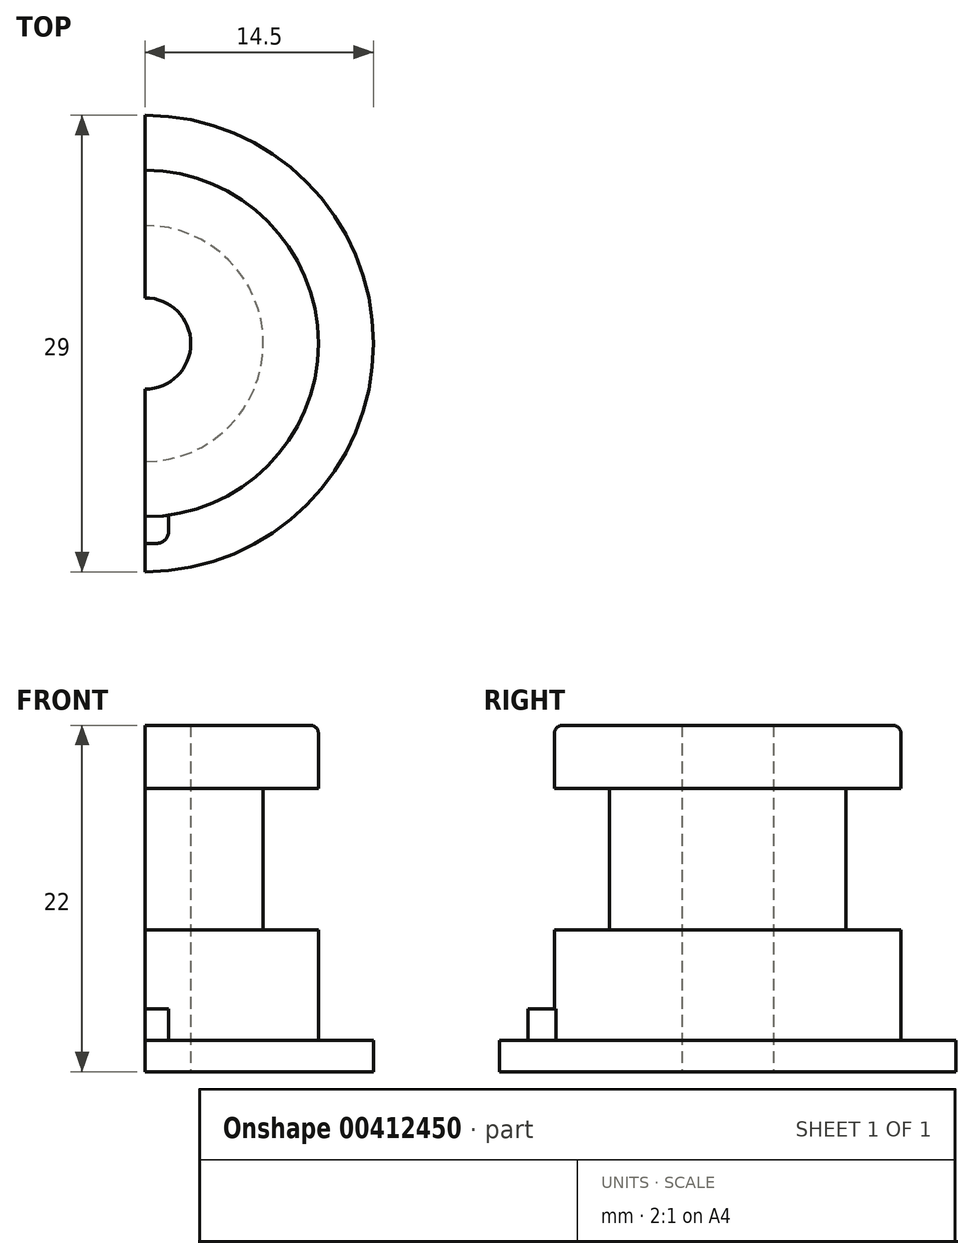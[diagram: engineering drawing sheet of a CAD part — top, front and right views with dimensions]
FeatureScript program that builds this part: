
annotation { "Feature Type Name" : "Feature", "Feature Type Description" : "" }
export const myFeature = defineFeature(function(context is Context, id is Id, definition is map)
    precondition{}
    {
        {
            var Q0;
            Q0=qCreatedBy(makeId("Top.planeOp"),FACE);
            var sketch = newSketch(context, id + "F0", { "sketchPlane" : qUnion([Q0])});
            skCircle(sketch, "E0", {"center": v(0, 0) * mm, "radius": 14.5 * mm});
            skSolve(sketch);
        }
        {
            var Q0;
            Q0=qSketchRegion(id+"F0",true);
            extrude(context, id + "F1", {"entities" : qUnion([Q0]), "depth" : 2 * mm});
        }
        {
            var Q0;
            Q0=makeQuery(id+"F1.opExtrude","CAP_FACE",FACE,{"disambiguationData":[OSD([sQuery(id+"F0.wireOp",EDGE,"E0")])],"isStart":false});
            var sketch = newSketch(context, id + "F2", { "sketchPlane" : qUnion([Q0])});
            skCircle(sketch, "E1", {"center": v(0, 0) * mm, "radius": 11 * mm});
            skSolve(sketch);
        }
        {
            var Q0;
            Q0=qSketchRegion(id+"F2",true);
            extrude(context, id + "F3", {"entities" : qUnion([Q0]), "operationType" : NewBodyOperationType.ADD, "depth" : 20 * mm});
        }
        {
            var Q0;
            Q0=makeQuery(id+"F1.opExtrude","CAP_FACE",FACE,{"disambiguationData":[OSD([sQuery(id+"F0.wireOp",EDGE,"E0")])],"isStart":true});
            var sketch = newSketch(context, id + "F4", { "sketchPlane" : qUnion([Q0])});
            skCircle(sketch, "E2", {"center": v(0, 0) * mm, "radius": 2.9 * mm});
            skSolve(sketch);
        }
        {
            var Q0;
            Q0=qSketchRegion(id+"F4",true);
            extrude(context, id + "F5", {"entities" : qUnion([Q0]), "operationType" : NewBodyOperationType.REMOVE, "endBound" : BoundingType.THROUGH_ALL, "oppositeDirection" : true, "depth" : 25 * mm});
        }
        {
            var Q0;
            Q0=makeQuery(id+"F1.opExtrude","CAP_FACE",FACE,{"disambiguationData":[OSD([sQuery(id+"F0.wireOp",EDGE,"E0")])],"isStart":false});
            var sketch = newSketch(context, id + "F6", { "sketchPlane" : qUnion([Q0])});
            skLineSegment(sketch, "E3.bottom", {"start": v(-1.5, -9.3) * mm, "end": v(1.5, -9.3) * mm});
            skLineSegment(sketch, "E3.top", {"start": v(-1.5, -12.7) * mm, "end": v(1.5, -12.7) * mm});
            skLineSegment(sketch, "E3.left", {"start": v(-1.5, -9.3) * mm, "end": v(-1.5, -12.7) * mm});
            skLineSegment(sketch, "E3.right", {"start": v(1.5, -9.3) * mm, "end": v(1.5, -12.7) * mm});
            skPoint(sketch, "E3.middle", {"position": v(0, -11) * mm});
            skSolve(sketch);
        }
        {
            var Q0;
            {var subQ0=sQuery(id+"F6.wireOp",EDGE,"E3.top");Q0=makeQuery(id+"F6.imprint","IMPRINT",FACE,{"disambiguationData":[TD([[makeQuery(id+"F6.imprint","IMPRINT",EDGE,{"derivedFrom":subQ0}),1.0]])]});}
            extrude(context, id + "F7", {"entities" : qUnion([Q0]), "operationType" : NewBodyOperationType.ADD, "depth" : 2 * mm});
        }
        {
            var Q0;
            Q0=makeQuery(id+"F7.opExtrude","SWEPT_EDGE",EDGE,{"disambiguationData":[OSD([sQuery(id+"F6.wireOp",EDGE,"E3.top"),sQuery(id+"F6.wireOp",EDGE,"E3.left")])]});
            var Q1;
            Q1=makeQuery(id+"F7.opExtrude","SWEPT_EDGE",EDGE,{"disambiguationData":[OSD([sQuery(id+"F6.wireOp",EDGE,"E3.top"),sQuery(id+"F6.wireOp",EDGE,"E3.right")])]});
            fillet(context, id + "F8", {"entities" : qUnion([Q0, Q1]), "radius" : 0.8 * mm, "tangentPropagation" : true, "allowEdgeOverflow" : false});
        }
        {
            var Q0;
            Q0=makeQuery(id+"F3.opExtrude","CAP_EDGE",EDGE,{"disambiguationData":[OSD([sQuery(id+"F2.wireOp",EDGE,"E1")])],"isStart":false});
            fillet(context, id + "F9", {"entities" : qUnion([Q0]), "radius" : 0.5 * mm, "tangentPropagation" : true, "allowEdgeOverflow" : false});
        }
        {
            var Q0;
            Q0=qCreatedBy(makeId("Front.planeOp"),FACE);
            var sketch = newSketch(context, id + "F10", { "sketchPlane" : qUnion([Q0])});
            skLineSegment(sketch, "E4", {"start": v(11, 2) * mm, "end": v(11, 4.1) * mm});
            skLineSegment(sketch, "E5", {"start": v(11, 4.1) * mm, "end": v(9.18, 3.05) * mm});
            skLineSegment(sketch, "E6", {"start": v(9.18, 3.05) * mm, "end": v(11, 2) * mm});
            skSolve(sketch);
        }
        {
            var Q0;
            Q0=qCreatedBy(makeId("Top.planeOp"),FACE);
            var sketch = newSketch(context, id + "F11", { "sketchPlane" : qUnion([Q0])});
            skLineSegment(sketch, "E7.bottom", {"start": v(0, 29.64) * mm, "end": v(-28.85, 29.64) * mm});
            skLineSegment(sketch, "E7.top", {"start": v(0, -24.5) * mm, "end": v(-28.85, -24.5) * mm});
            skLineSegment(sketch, "E7.left", {"start": v(0, 29.64) * mm, "end": v(0, -24.5) * mm});
            skLineSegment(sketch, "E7.right", {"start": v(-28.85, 29.64) * mm, "end": v(-28.85, -24.5) * mm});
            skSolve(sketch);
        }
        {
            var Q0;
            Q0=qSketchRegion(id+"F11",true);
            extrude(context, id + "F12", {"entities" : qUnion([Q0]), "operationType" : NewBodyOperationType.REMOVE, "endBound" : BoundingType.THROUGH_ALL, "depth" : 25 * mm});
        }
        {
            var Q0;
            Q0=qCreatedBy(makeId("Right.planeOp"),FACE);
            var sketch = newSketch(context, id + "F13", { "sketchPlane" : qUnion([Q0])});
            skLineSegment(sketch, "E8", {"start": v(0, 0) * mm, "end": v(0, 26.62) * mm});
            skSolve(sketch);
        }
        {
            var Q0;
            Q0=qCreatedBy(makeId("Front.planeOp"),FACE);
            var sketch = newSketch(context, id + "F14", { "sketchPlane" : qUnion([Q0])});
            skLineSegment(sketch, "E9.bottom", {"start": v(11, 18) * mm, "end": v(7.5, 18) * mm});
            skLineSegment(sketch, "E9.top", {"start": v(11, 9) * mm, "end": v(7.5, 9) * mm});
            skLineSegment(sketch, "E9.left", {"start": v(11, 18) * mm, "end": v(11, 9) * mm});
            skLineSegment(sketch, "E9.right", {"start": v(7.5, 18) * mm, "end": v(7.5, 9) * mm});
            skSolve(sketch);
        }
        {
            var Q0;
            Q0 = qSketchRegion(id + "F14", true);
            var Q1;
            Q1=sQuery(id+"F13.wireOp",EDGE,"E8");
            revolve(context, id + "F15", {"operationType" : NewBodyOperationType.REMOVE, "entities" : qUnion([Q0]), "axis" : qUnion([Q1]), "revolveType" : RevolveType.FULL});
        }
    });
